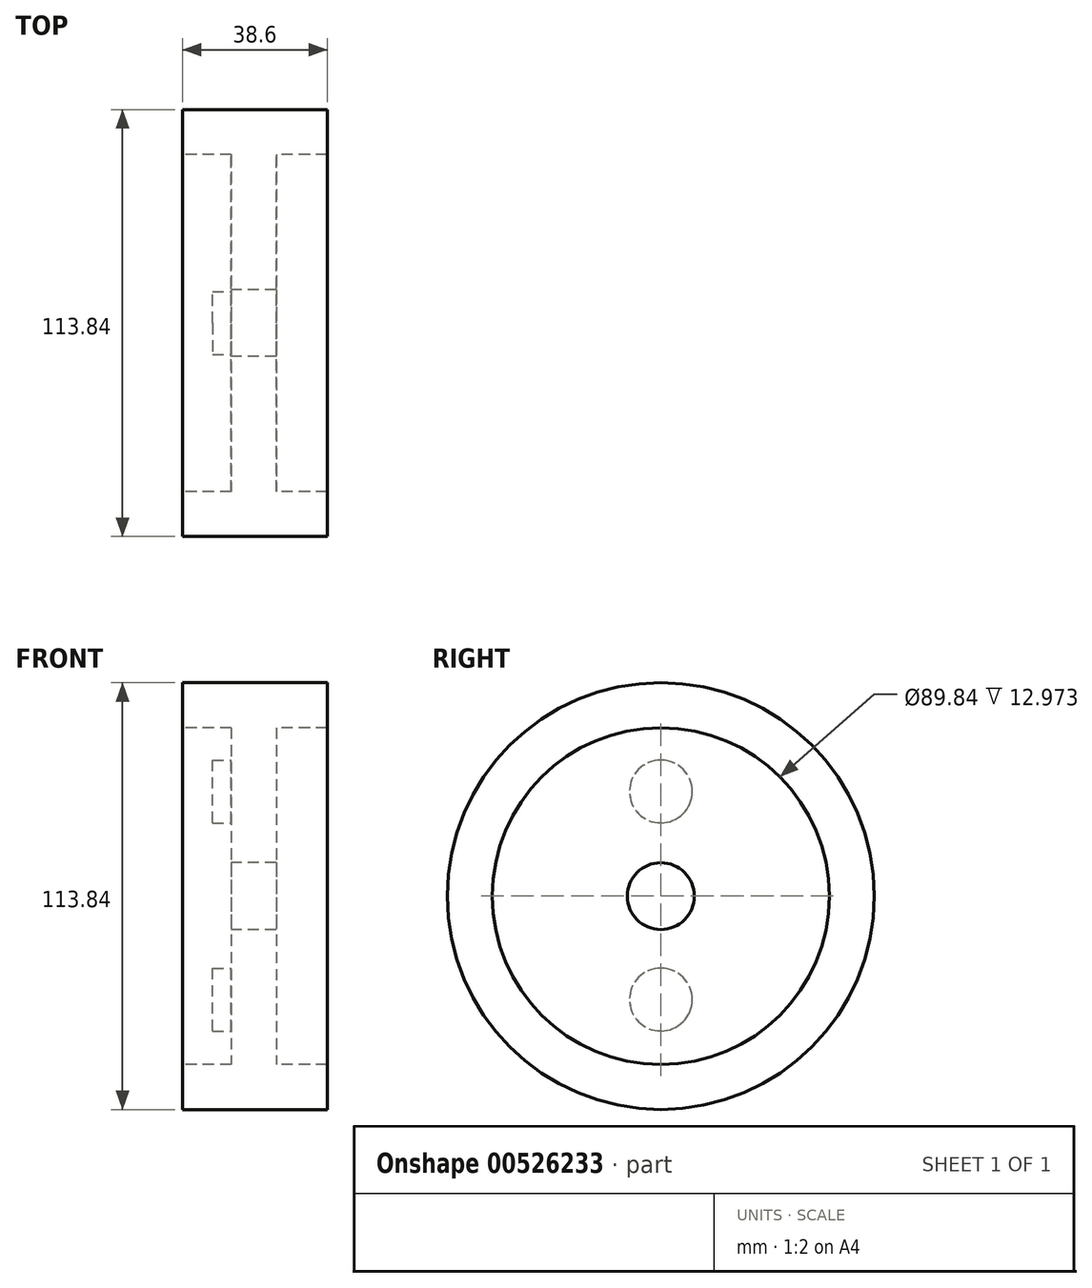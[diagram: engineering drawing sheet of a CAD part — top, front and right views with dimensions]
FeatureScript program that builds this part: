
annotation { "Feature Type Name" : "Feature", "Feature Type Description" : "" }
export const myFeature = defineFeature(function(context is Context, id is Id, definition is map)
    precondition{}
    {
        {
            var Q0;
            Q0=qCreatedBy(makeId("Top.planeOp"),FACE);
            var sketch = newSketch(context, id + "F0", { "sketchPlane" : qUnion([Q0])});
            skLineSegment(sketch, "E0.bottom", {"start": v(-6.49, 44.92) * mm, "end": v(5.51, 44.92) * mm});
            skLineSegment(sketch, "E0.top", {"start": v(-6.49, 8.92) * mm, "end": v(5.51, 8.92) * mm});
            skLineSegment(sketch, "E0.left", {"start": v(-6.49, 44.92) * mm, "end": v(-6.49, 8.92) * mm});
            skLineSegment(sketch, "E0.right", {"start": v(5.51, 44.92) * mm, "end": v(5.51, 8.92) * mm});
            skLineSegment(sketch, "E1.bottom", {"start": v(-19.46, 56.92) * mm, "end": v(19.14, 56.92) * mm});
            skLineSegment(sketch, "E1.top", {"start": v(-19.46, 44.92) * mm, "end": v(19.14, 44.92) * mm});
            skLineSegment(sketch, "E1.left", {"start": v(-19.46, 56.92) * mm, "end": v(-19.46, 44.92) * mm});
            skLineSegment(sketch, "E1.right", {"start": v(19.14, 56.92) * mm, "end": v(19.14, 44.92) * mm});
            skLineSegment(sketch, "E2", {"start": v(-17.51, 0) * mm, "end": v(23.03, 0) * mm});
            skSolve(sketch);
        }
        {
            var Q0;
            Q0 = qSketchRegion(id + "F0", true);
            var Q1;
            Q1=sQuery(id+"F0.wireOp",EDGE,"E2");
            revolve(context, id + "F1", {"entities" : qUnion([Q0]), "axis" : qUnion([Q1]), "revolveType" : RevolveType.FULL});
        }
        {
            var Q0;
            Q0=makeQuery(id+"F1.opRevolve","SWEPT_FACE",FACE,{"disambiguationData":[OSD([sQuery(id+"F0.wireOp",EDGE,"E0.left")])]});
            var sketch = newSketch(context, id + "F2", { "sketchPlane" : qUnion([Q0])});
            skCircle(sketch, "E3", {"center": v(0, 27.9) * mm, "radius": 8.37 * mm});
            skCircle(sketch, "E4", {"center": v(0, -27.59) * mm, "radius": 8.37 * mm});
            skSolve(sketch);
        }
        {
            var Q0;
            Q0=makeQuery(id+"F2.imprint","IMPRINT",FACE,{"disambiguationData":[TD([[makeQuery(id+"F2.imprint","IMPRINT",EDGE,{"derivedFrom":sQuery(id+"F2.wireOp",EDGE,"E3")}),1.0]])]});
            var Q1;
            Q1=makeQuery(id+"F2.imprint","IMPRINT",FACE,{"disambiguationData":[TD([[makeQuery(id+"F2.imprint","IMPRINT",EDGE,{"derivedFrom":sQuery(id+"F2.wireOp",EDGE,"E4")}),1.0]])]});
            extrude(context, id + "F3", {"entities" : qUnion([Q0, Q1]), "operationType" : NewBodyOperationType.ADD, "depth" : 5 * mm, "offsetDistance" : 25 * mm});
        }
    });
